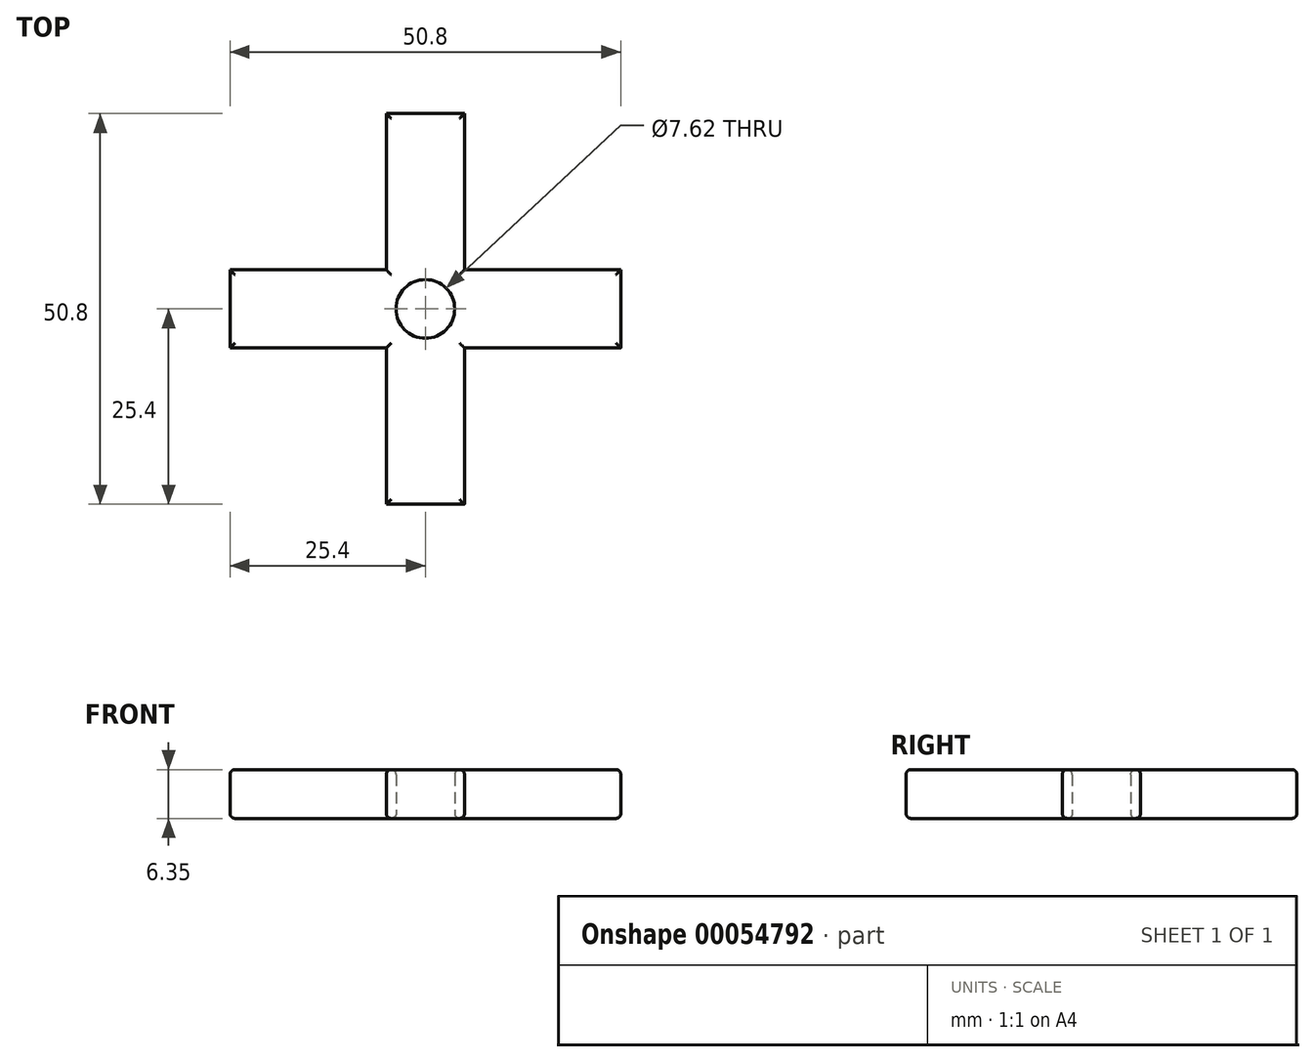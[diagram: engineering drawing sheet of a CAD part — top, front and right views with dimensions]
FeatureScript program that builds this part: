
annotation { "Feature Type Name" : "Feature", "Feature Type Description" : "" }
export const myFeature = defineFeature(function(context is Context, id is Id, definition is map)
    precondition{}
    {
        {
            var Q0;
            Q0=qCreatedBy(makeId("Top.planeOp"),FACE);
            var sketch = newSketch(context, id + "F0", { "sketchPlane" : qUnion([Q0])});
            skCircle(sketch, "E0", {"center": v(0, 0) * mm, "radius": 3.81 * mm});
            skCircle(sketch, "E1", {"center": v(0, 0) * mm, "radius": 6.35 * mm});
            skSolve(sketch);
        }
        {
            var Q0;
            Q0 = qSketchRegion(id + "F0", true);
            extrude(context, id + "F1", {"entities" : qUnion([Q0]), "depth" : 6.35 * mm});
        }
        {
            var Q0;
            Q0=makeQuery(id+"F1.opExtrude","CAP_FACE",FACE,{"disambiguationData":[OSD([sQuery(id+"F0.wireOp",EDGE,"E0"),sQuery(id+"F0.wireOp",EDGE,"E1")])],"isStart":false});
            var sketch = newSketch(context, id + "F2", { "sketchPlane" : qUnion([Q0])});
            skLineSegment(sketch, "E2", {"start": v(25.4, 5.08) * mm, "end": v(25.4, -5.08) * mm});
            skLineSegment(sketch, "E3", {"start": v(-25.4, 5.08) * mm, "end": v(-25.4, -5.08) * mm});
            skPoint(sketch, "E3.startSnap0", {"position": v(-25.4, 5.27) * mm});
            skLineSegment(sketch, "E4", {"start": v(-5.08, -25.4) * mm, "end": v(5.08, -25.4) * mm});
            skLineSegment(sketch, "E5", {"start": v(5.08, 25.4) * mm, "end": v(-5.08, 25.4) * mm});
            skLineSegment(sketch, "E6", {"start": v(-25.4, 5.08) * mm, "end": v(-3.81, 5.08) * mm});
            skLineSegment(sketch, "E7", {"start": v(-25.4, -5.08) * mm, "end": v(-3.8, -5.08) * mm});
            skLineSegment(sketch, "E8", {"start": v(-3.8, -5.08) * mm, "end": v(-3.81, 5.08) * mm});
            skLineSegment(sketch, "E9", {"start": v(-5.08, 25.4) * mm, "end": v(-5.08, 3.8) * mm});
            skLineSegment(sketch, "E10", {"start": v(-5.08, 3.8) * mm, "end": v(5.08, 3.8) * mm});
            skLineSegment(sketch, "E11", {"start": v(5.08, 3.8) * mm, "end": v(5.08, 25.4) * mm});
            skLineSegment(sketch, "E12", {"start": v(25.4, 5.08) * mm, "end": v(3.8, 5.08) * mm});
            skLineSegment(sketch, "E13", {"start": v(3.8, 5.08) * mm, "end": v(3.81, -5.08) * mm});
            skLineSegment(sketch, "E14", {"start": v(3.8, -5.08) * mm, "end": v(25.4, -5.08) * mm});
            skLineSegment(sketch, "E15", {"start": v(5.08, -25.4) * mm, "end": v(5.08, -3.8) * mm});
            skLineSegment(sketch, "E16", {"start": v(5.08, -3.8) * mm, "end": v(-5.08, -3.8) * mm});
            skLineSegment(sketch, "E17", {"start": v(-5.08, -3.8) * mm, "end": v(-5.08, -25.4) * mm});
            skSolve(sketch);
        }
        {
            var Q0;
            Q0 = qSketchRegion(id + "F2", true);
            extrude(context, id + "F3", {"entities" : qUnion([Q0]), "operationType" : NewBodyOperationType.ADD, "oppositeDirection" : true, "depth" : 6.35 * mm});
        }
        {
            var Q0;
            Q0=makeQuery(id+"F1.opExtrude","CAP_EDGE",EDGE,{"disambiguationData":[OSD([sQuery(id+"F0.wireOp",EDGE,"E0")])],"isStart":false});
            var Q1;
            Q1=makeQuery(id+"F1.opExtrude","CAP_EDGE",EDGE,{"disambiguationData":[OSD([sQuery(id+"F0.wireOp",EDGE,"E0")])],"isStart":true});
            var Q2;
            Q2=makeQuery(id+"F3.boolean.opBoolean","MERGE",FACE,{"derivedFrom":[makeQuery(id+"F1.opExtrude","CAP_FACE",FACE,{"disambiguationData":[OSD([sQuery(id+"F0.wireOp",EDGE,"E0"),sQuery(id+"F0.wireOp",EDGE,"E1")])],"isStart":true}),makeQuery(id+"F3.opExtrude","CAP_FACE",FACE,{"disambiguationData":[OSD([sQuery(id+"F2.wireOp",EDGE,"E2"),sQuery(id+"F2.wireOp",EDGE,"E3"),sQuery(id+"F2.wireOp",EDGE,"E4"),sQuery(id+"F2.wireOp",EDGE,"E5"),sQuery(id+"F2.wireOp",EDGE,"E6"),sQuery(id+"F2.wireOp",EDGE,"E7"),sQuery(id+"F2.wireOp",EDGE,"E8"),sQuery(id+"F2.wireOp",EDGE,"E9"),sQuery(id+"F2.wireOp",EDGE,"E10"),sQuery(id+"F2.wireOp",EDGE,"E11"),sQuery(id+"F2.wireOp",EDGE,"E12"),sQuery(id+"F2.wireOp",EDGE,"E13"),sQuery(id+"F2.wireOp",EDGE,"E14"),sQuery(id+"F2.wireOp",EDGE,"E15"),sQuery(id+"F2.wireOp",EDGE,"E16"),sQuery(id+"F2.wireOp",EDGE,"E17")])],"isStart":false})]});
            var Q3;
            Q3=makeQuery(id+"F3.boolean.opBoolean","MERGE",FACE,{"derivedFrom":[makeQuery(id+"F1.opExtrude","CAP_FACE",FACE,{"disambiguationData":[OSD([sQuery(id+"F0.wireOp",EDGE,"E0"),sQuery(id+"F0.wireOp",EDGE,"E1")])],"isStart":false}),makeQuery(id+"F3.opExtrude","CAP_FACE",FACE,{"disambiguationData":[OSD([sQuery(id+"F2.wireOp",EDGE,"E2"),sQuery(id+"F2.wireOp",EDGE,"E3"),sQuery(id+"F2.wireOp",EDGE,"E4"),sQuery(id+"F2.wireOp",EDGE,"E5"),sQuery(id+"F2.wireOp",EDGE,"E6"),sQuery(id+"F2.wireOp",EDGE,"E7"),sQuery(id+"F2.wireOp",EDGE,"E8"),sQuery(id+"F2.wireOp",EDGE,"E9"),sQuery(id+"F2.wireOp",EDGE,"E10"),sQuery(id+"F2.wireOp",EDGE,"E11"),sQuery(id+"F2.wireOp",EDGE,"E12"),sQuery(id+"F2.wireOp",EDGE,"E13"),sQuery(id+"F2.wireOp",EDGE,"E14"),sQuery(id+"F2.wireOp",EDGE,"E15"),sQuery(id+"F2.wireOp",EDGE,"E16"),sQuery(id+"F2.wireOp",EDGE,"E17")])],"isStart":true})]});
            fillet(context, id + "F4", {"entities" : qUnion([Q0, Q1, Q2, Q3]), "radius" : 0.64 * mm, "tangentPropagation" : true, "allowEdgeOverflow" : false});
        }
    });
